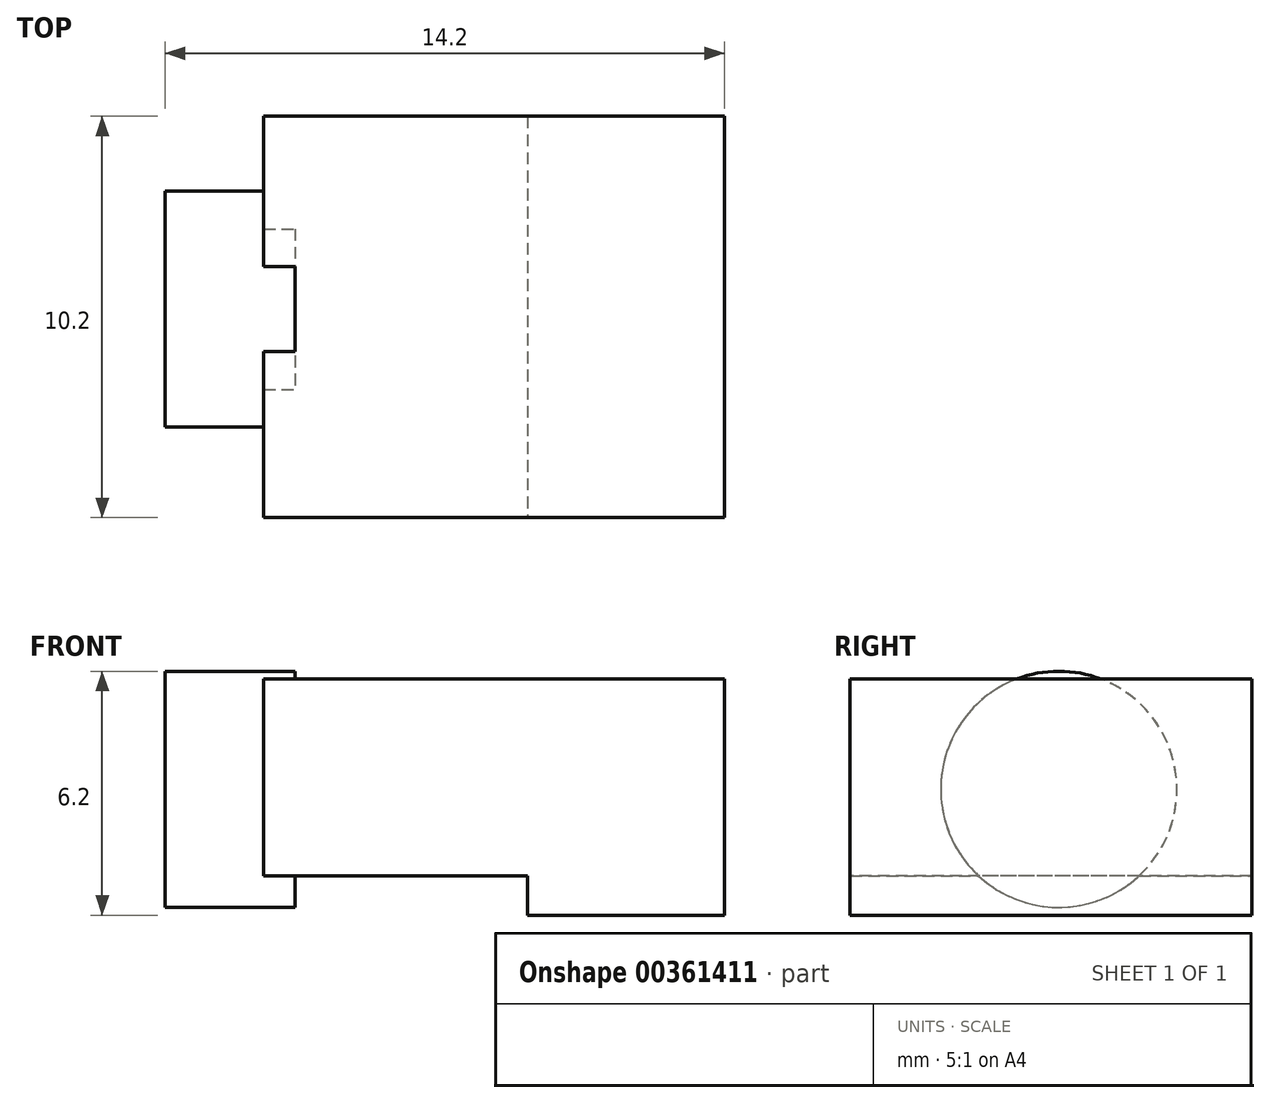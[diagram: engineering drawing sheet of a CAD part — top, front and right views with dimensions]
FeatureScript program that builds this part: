
annotation { "Feature Type Name" : "Feature", "Feature Type Description" : "" }
export const myFeature = defineFeature(function(context is Context, id is Id, definition is map)
    precondition{}
    {
        {
            var Q0;
            Q0=qCreatedBy(makeId("Top.planeOp"),FACE);
            var sketch = newSketch(context, id + "F0", { "sketchPlane" : qUnion([Q0])});
            skLineSegment(sketch, "E0", {"start": v(0, -5.3) * mm, "end": v(0, 4.9) * mm});
            skLineSegment(sketch, "E1", {"start": v(11.7, 4.9) * mm, "end": v(0, 4.9) * mm});
            skLineSegment(sketch, "E2", {"start": v(11.7, 4.9) * mm, "end": v(11.7, -5.3) * mm});
            skLineSegment(sketch, "E3", {"start": v(0, -5.3) * mm, "end": v(11.7, -5.3) * mm});
            skLineSegment(sketch, "E4", {"start": v(6.7, 4.9) * mm, "end": v(6.7, -5.3) * mm});
            skSolve(sketch);
        }
        {
            var Q0;
            {var subQ0=sQuery(id+"F0.wireOp",EDGE,"E2");Q0=makeQuery(id+"F0.imprint","IMPRINT",FACE,{"disambiguationData":[TD([[makeQuery(id+"F0.imprint","IMPRINT",EDGE,{"derivedFrom":subQ0}),-1.0]])]});}
            var Q1;
            {var subQ0=sQuery(id+"F0.wireOp",EDGE,"E0");Q1=makeQuery(id+"F0.imprint","IMPRINT",FACE,{"disambiguationData":[TD([[makeQuery(id+"F0.imprint","IMPRINT",EDGE,{"derivedFrom":subQ0}),-1.0]])]});}
            extrude(context, id + "F1", {"entities" : qUnion([Q0, Q1]), "depth" : 5 * mm});
        }
        {
            var Q0;
            {var subQ0=sQuery(id+"F0.wireOp",EDGE,"E2");Q0=makeQuery(id+"F0.imprint","IMPRINT",FACE,{"disambiguationData":[TD([[makeQuery(id+"F0.imprint","IMPRINT",EDGE,{"derivedFrom":subQ0}),-1.0]])]});}
            extrude(context, id + "F2", {"entities" : qUnion([Q0]), "operationType" : NewBodyOperationType.ADD, "oppositeDirection" : true, "depth" : 1 * mm});
        }
        {
            var Q0;
            Q0=makeQuery(id+"F1.opExtrude","SWEPT_FACE",FACE,{"disambiguationData":[OSD([sQuery(id+"F0.wireOp",EDGE,"E0")])]});
            var sketch = newSketch(context, id + "F3", { "sketchPlane" : qUnion([Q0])});
            skLineSegment(sketch, "E5", {"start": v(0, 0) * mm, "end": v(0, 5) * mm, "construction": true});
            skCircle(sketch, "E6", {"center": v(0, 2.2) * mm, "radius": 3 * mm});
            skSolve(sketch);
        }
        {
            var Q0;
            {var subQ0=sQuery(id+"F3.wireOp",EDGE,"E6");var subQ1=sQuery(id+"F0.wireOp",EDGE,"E0");var subQ2=makeQuery(id+"F1.opExtrude","CAP_EDGE",EDGE,{"disambiguationData":[OSD([subQ1])],"isStart":false});var subQ3=makeQuery(id+"F3.imprint","INTERSECT",VERTEX,{"disambiguationData":[OD(0.0)],"derivedFrom":[subQ2,subQ0]});Q0=makeQuery(id+"F3.imprint","IMPRINT",FACE,{"disambiguationData":[TD([[makeQuery(id+"F3.imprint","IMPRINT",EDGE,{"disambiguationData":[TD([[subQ3,-1.0]])],"derivedFrom":subQ0}),1.0]])]});}
            var Q1;
            {var subQ0=sQuery(id+"F3.wireOp",EDGE,"E6");var subQ1=makeQuery(id+"F1.opExtrude","CAP_EDGE",EDGE,{"disambiguationData":[OSD([sQuery(id+"F0.wireOp",EDGE,"E0")])],"isStart":false});var subQ2=makeQuery(id+"F3.imprint","INTERSECT",VERTEX,{"disambiguationData":[OD(0.0)],"derivedFrom":[subQ1,subQ0]});Q1=makeQuery(id+"F3.imprint","IMPRINT",FACE,{"disambiguationData":[TD([[makeQuery(id+"F3.imprint","IMPRINT",EDGE,{"disambiguationData":[TD([[subQ2,1.0]])],"derivedFrom":subQ0}),1.0]])]});}
            var Q2;
            {var subQ0=sQuery(id+"F3.wireOp",EDGE,"E6");var subQ1=makeQuery(id+"F1.opExtrude","CAP_EDGE",EDGE,{"disambiguationData":[OSD([sQuery(id+"F0.wireOp",EDGE,"E0")])],"isStart":true});var subQ2=makeQuery(id+"F3.imprint","INTERSECT",VERTEX,{"disambiguationData":[OD(0.0)],"derivedFrom":[subQ1,subQ0]});Q2=makeQuery(id+"F3.imprint","IMPRINT",FACE,{"disambiguationData":[TD([[makeQuery(id+"F3.imprint","IMPRINT",EDGE,{"disambiguationData":[TD([[subQ2,-1.0]])],"derivedFrom":subQ0}),1.0]])]});}
            extrude(context, id + "F4", {"entities" : qUnion([Q0, Q1, Q2]), "operationType" : NewBodyOperationType.ADD, "depth" : 2.5 * mm, "hasSecondDirection" : true, "secondDirectionOppositeDirection" : true, "secondDirectionDepth" : .8 * mm});
        }
    });
